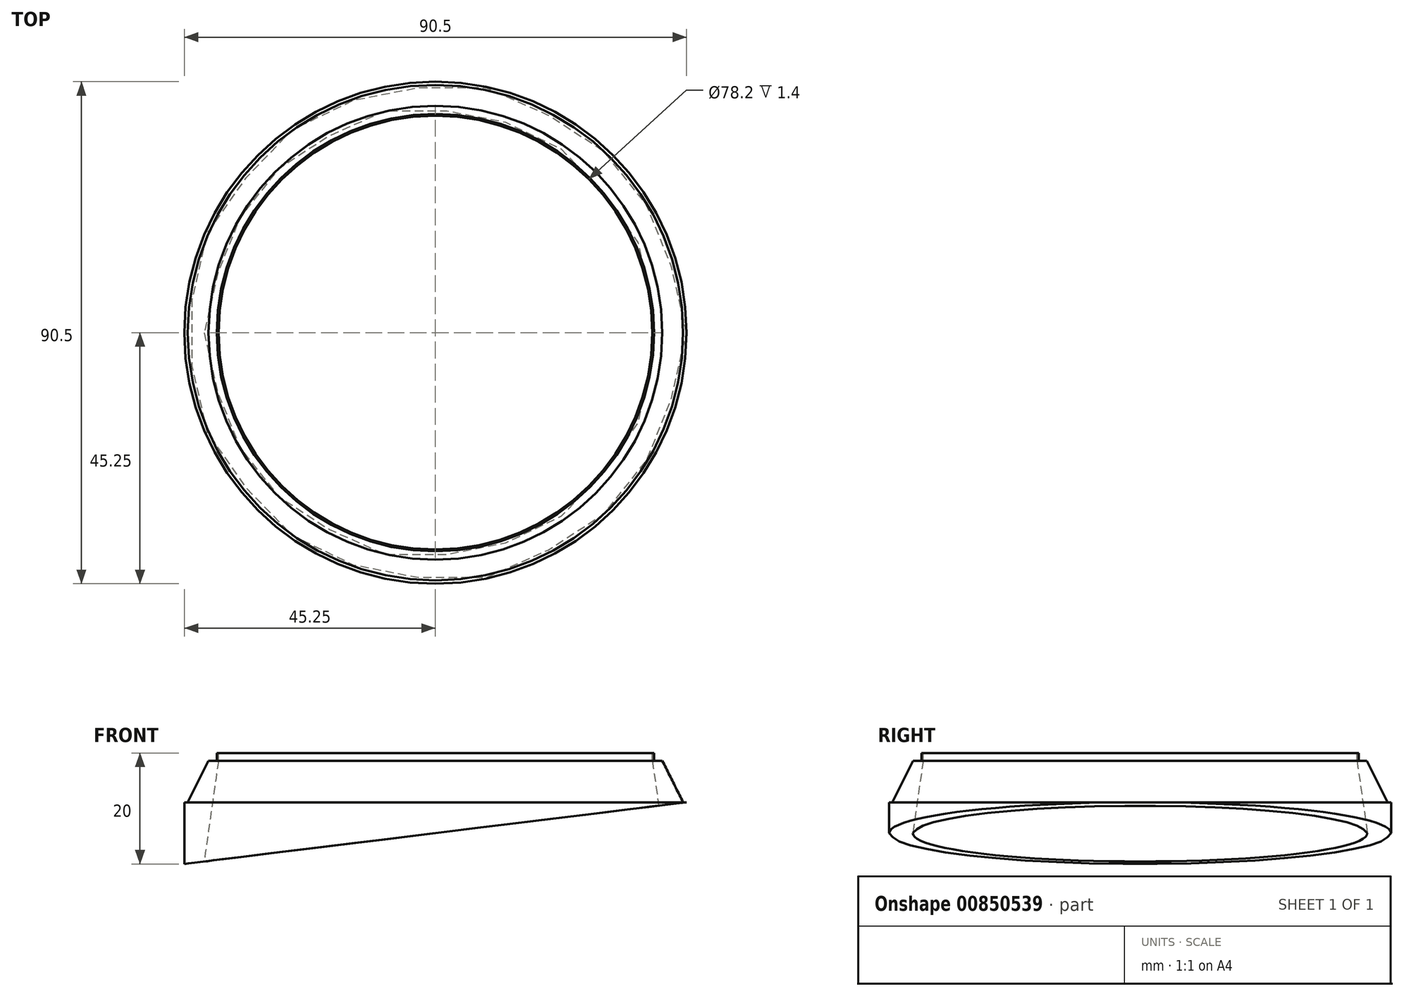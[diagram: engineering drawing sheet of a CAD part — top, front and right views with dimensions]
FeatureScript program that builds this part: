
annotation { "Feature Type Name" : "Feature", "Feature Type Description" : "" }
export const myFeature = defineFeature(function(context is Context, id is Id, definition is map)
    precondition{}
    {
        {
            var Q0;
            Q0=qCreatedBy(makeId("Front.planeOp"),FACE);
            var sketch = newSketch(context, id + "F0", { "sketchPlane" : qUnion([Q0])});
            skLineSegment(sketch, "E0", {"start": v(-39.4, 20) * mm, "end": v(-39.4, 18.6) * mm});
            skLineSegment(sketch, "E1", {"start": v(-39.4, 18.6) * mm, "end": v(-40.9, 18.6) * mm});
            skLineSegment(sketch, "E2", {"start": v(-40.9, 18.6) * mm, "end": v(-44.64, 11.12) * mm});
            skLineSegment(sketch, "E3", {"start": v(-44.64, 11.12) * mm, "end": v(-45.25, 11.12) * mm});
            skLineSegment(sketch, "E4", {"start": v(-45.25, 11.12) * mm, "end": v(-45.25, 0) * mm});
            skLineSegment(sketch, "E5", {"start": v(-45.25, 0) * mm, "end": v(-41.75, 0) * mm});
            skLineSegment(sketch, "E6", {"start": v(-41.75, 0) * mm, "end": v(-39.1, 18.6) * mm});
            skLineSegment(sketch, "E7", {"start": v(-39.1, 18.6) * mm, "end": v(-39.1, 20) * mm});
            skLineSegment(sketch, "E8", {"start": v(-39.4, 20) * mm, "end": v(-39.1, 20) * mm});
            skLineSegment(sketch, "E9", {"start": v(-39.1, 20) * mm, "end": v(0, 20) * mm, "construction": true});
            skSolve(sketch);
        }
        {
            var Q0;
            Q0=qCreatedBy(makeId("Front.planeOp"),FACE);
            var sketch = newSketch(context, id + "F1", { "sketchPlane" : qUnion([Q0])});
            skLineSegment(sketch, "E10", {"start": v(0, 32.97) * mm, "end": v(0, -14.82) * mm});
            skSolve(sketch);
        }
        {
            var Q0;
            Q0 = qSketchRegion(id + "F0", true);
            var Q1;
            Q1=sQuery(id+"F1.wireOp",EDGE,"E10");
            revolve(context, id + "F2", {"surfaceOperationType" : NewSurfaceOperationType.NEW, "entities" : qUnion([Q0]), "axis" : qUnion([Q1]), "revolveType" : RevolveType.FULL});
        }
        {
            var Q0;
            Q0=qCreatedBy(makeId("Front.planeOp"),FACE);
            var sketch = newSketch(context, id + "F3", { "sketchPlane" : qUnion([Q0])});
            skLineSegment(sketch, "E11", {"start": v(-45.25, 11.12) * mm, "end": v(-45.25, 0) * mm, "construction": true});
            skLineSegment(sketch, "E12", {"start": v(-45.25, 0) * mm, "end": v(45.25, 11.12) * mm});
            skLineSegment(sketch, "E13", {"start": v(45.25, 11.12) * mm, "end": v(-45.25, 11.12) * mm, "construction": true});
            skLineSegment(sketch, "E14", {"start": v(45.25, 11.12) * mm, "end": v(46.62, 0) * mm});
            skLineSegment(sketch, "E15", {"start": v(46.62, 0) * mm, "end": v(-45.25, 0) * mm});
            skSolve(sketch);
        }
        {
            var Q0;
            Q0 = qSketchRegion(id + "F3", true);
            var Q1;
            Q1 = qConstructionFilter(qBodyType(qCreatedBy(id + "F3" ,EDGE), BodyType.WIRE), ConstructionObject.NO);
            extrude(context, id + "F4", {"entities" : qUnion([Q0]), "operationType" : NewBodyOperationType.REMOVE, "surfaceEntities" : qUnion([Q1]), "endBound" : BoundingType.THROUGH_ALL, "depth" : 25 * mm, "offsetDistance" : 25 * mm, "hasSecondDirection" : true, "secondDirectionBound" : SecondDirectionBoundingType.THROUGH_ALL, "secondDirectionOppositeDirection" : true, "secondDirectionDepth" : 25 * mm});
        }
    });
